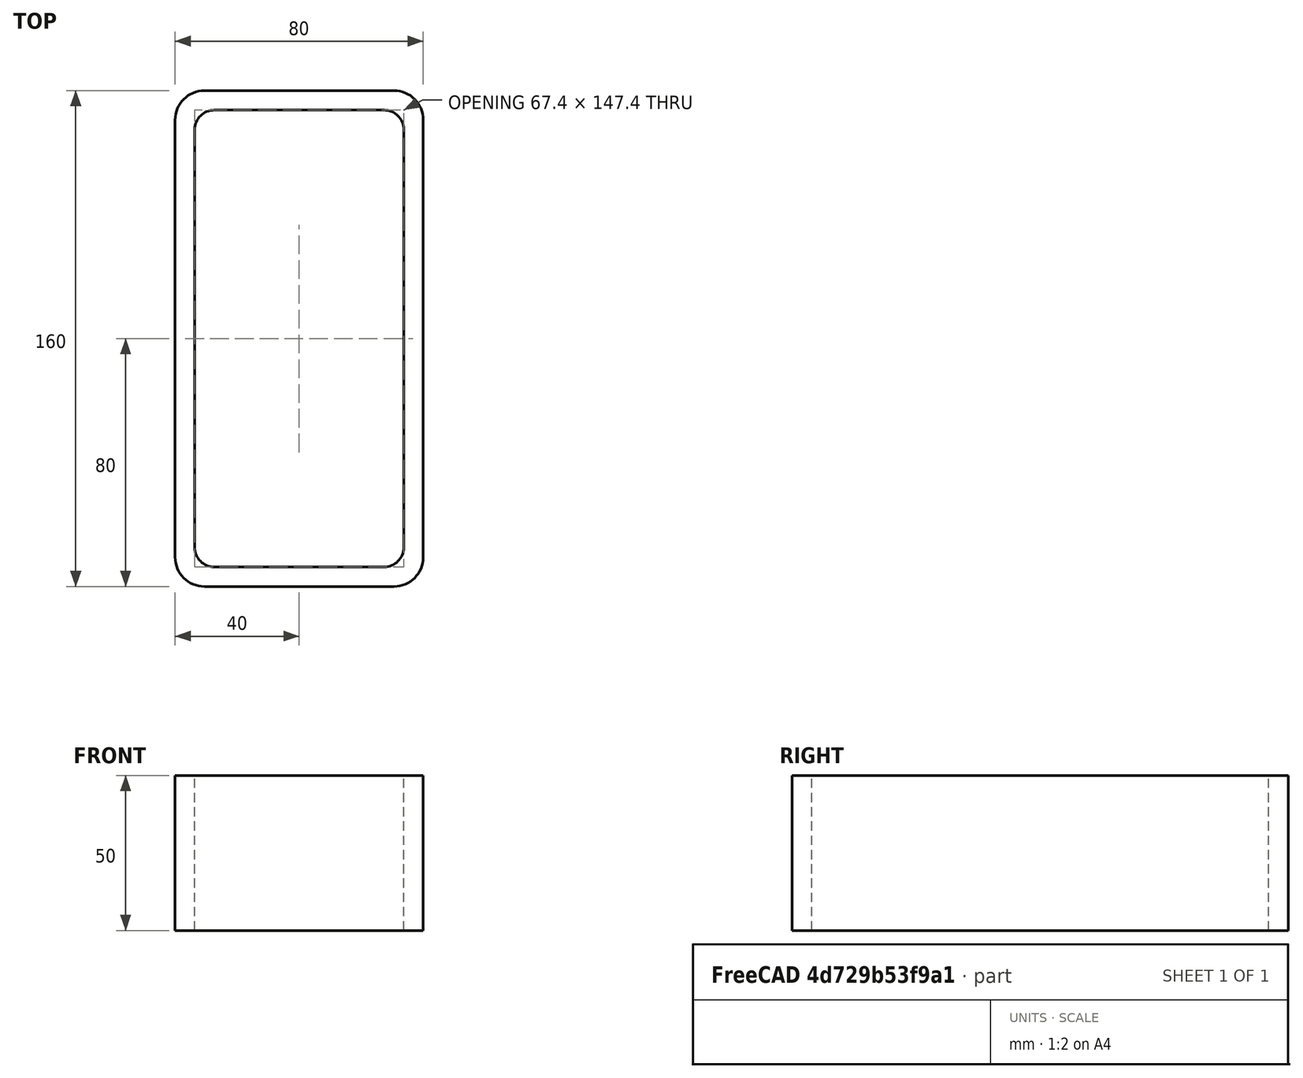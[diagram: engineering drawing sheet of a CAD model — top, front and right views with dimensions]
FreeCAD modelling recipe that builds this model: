
FCSTD DOCUMENT  (FreeCAD 0.15R4671 (Git))
Label: Rectangular hollow section 160x80x6.3 EN10219 S235JRH
License: All rights reserved
LicenseURL: http://en.wikipedia.org/wiki/All_rights_reserved
objects: Sketcher::SketchObject×1, Part::Extrusion×1
note: 2 computed .brp shape members not serialized (recipe doc carries the construction recipe); baked Part::Feature solids carry a one-line shape summary decoded from their .brp

FEATURE [Sketcher::SketchObject] Sketch
  sketch-geometry (16):
    g0: LineSegment StartX=-27.4 StartY=73.7 StartZ=0 EndX=27.4 EndY=73.7 EndZ=0
    g1: LineSegment StartX=33.7 StartY=67.4 StartZ=0 EndX=33.7 EndY=-67.4 EndZ=0
    g2: LineSegment StartX=27.4 StartY=-73.7 StartZ=0 EndX=-27.4 EndY=-73.7 EndZ=0
    g3: LineSegment StartX=-33.7 StartY=-67.4 StartZ=0 EndX=-33.7 EndY=67.4 EndZ=0
    g4: LineSegment StartX=-30.55 StartY=80 StartZ=0 EndX=30.55 EndY=80 EndZ=0
    g5: LineSegment StartX=40 StartY=70.55 StartZ=0 EndX=40 EndY=-70.55 EndZ=0
    g6: LineSegment StartX=30.55 StartY=-80 StartZ=0 EndX=-30.55 EndY=-80 EndZ=0
    g7: LineSegment StartX=-40 StartY=-70.55 StartZ=0 EndX=-40 EndY=70.55 EndZ=0
    g8: ArcOfCircle CenterX=-27.4 CenterY=67.4 CenterZ=0 NormalX=0 NormalY=0 NormalZ=1 Radius=6.3 StartAngle=1.5708 EndAngle=3.14159
    g9: ArcOfCircle CenterX=27.4 CenterY=67.4 CenterZ=0 NormalX=0 NormalY=0 NormalZ=1 Radius=6.3 StartAngle=0 EndAngle=1.5708
    g10: ArcOfCircle CenterX=27.4 CenterY=-67.4 CenterZ=0 NormalX=0 NormalY=0 NormalZ=1 Radius=6.3 StartAngle=4.71239 EndAngle=6.28319
    g11: ArcOfCircle CenterX=-27.4 CenterY=-67.4 CenterZ=0 NormalX=0 NormalY=0 NormalZ=1 Radius=6.3 StartAngle=3.14159 EndAngle=4.71239
    g12: ArcOfCircle CenterX=30.55 CenterY=70.55 CenterZ=0 NormalX=0 NormalY=0 NormalZ=1 Radius=9.45 StartAngle=0 EndAngle=1.5708
    g13: ArcOfCircle CenterX=30.55 CenterY=-70.55 CenterZ=0 NormalX=0 NormalY=0 NormalZ=1 Radius=9.45 StartAngle=4.71239 EndAngle=6.28319
    g14: ArcOfCircle CenterX=-30.55 CenterY=-70.55 CenterZ=0 NormalX=0 NormalY=0 NormalZ=1 Radius=9.45 StartAngle=3.14159 EndAngle=4.71239
    g15: ArcOfCircle CenterX=-30.55 CenterY=70.55 CenterZ=0 NormalX=0 NormalY=0 NormalZ=1 Radius=9.45 StartAngle=1.5708 EndAngle=3.14159
  constraints (36):
    c: Horizontal(g2)
    c: Vertical(g3)
    c: Horizontal(g6)
    c: Vertical(g7)
    c: Tangent(g3,g8) = 1.5708
    c: Tangent(g0,g8) = 1.5708
    c: Tangent(g0,g9) = 1.5708
    c: Tangent(g1,g9) = 1.5708
    c: Tangent(g1,g10) = 1.5708
    c: Tangent(g2,g10) = 1.5708
    c: Tangent(g2,g11) = 1.5708
    c: Tangent(g3,g11) = 1.5708
    c: Tangent(g4,g12) = 1.5708
    c: Tangent(g5,g12) = 1.5708
    c: Tangent(g5,g13) = 1.5708
    c: Tangent(g6,g13) = 1.5708
    c: Tangent(g6,g14) = 1.5708
    c: Tangent(g7,g14) = 1.5708
    c: Tangent(g7,g15) = 1.5708
    c: Tangent(g4,g15) = 1.5708
    c: Equal(g9,g8)
    c: Equal(g9,g11)
    c: Equal(g9,g10)
    c: Equal(g12,g15)
    c: Equal(g12,g14)
    c: Equal(g12,g13)
    c: Symmetric(g4,g6,g-1)
    c: Symmetric(g7,g5,g-2)
    c: DistanceY(g4,g6) = -160
    c: DistanceX(g7,g5) = 80
    c: Symmetric(g3,g1,g-2)
    c: Symmetric(g0,g2,g-1)
    c: DistanceY(g0,g4) = 6.3
    c: DistanceX(g5,g1) = -6.3
    c: Radius(g9) = 6.3
    c: Radius(g12) = 9.45
FEATURE [Part::Extrusion] Extrude  label="Rectangular hollow section 160x80x6.3 EN10219 S235JRH"
  Base = -> Sketch
  Dir = (0,0,50)
  Solid = true
